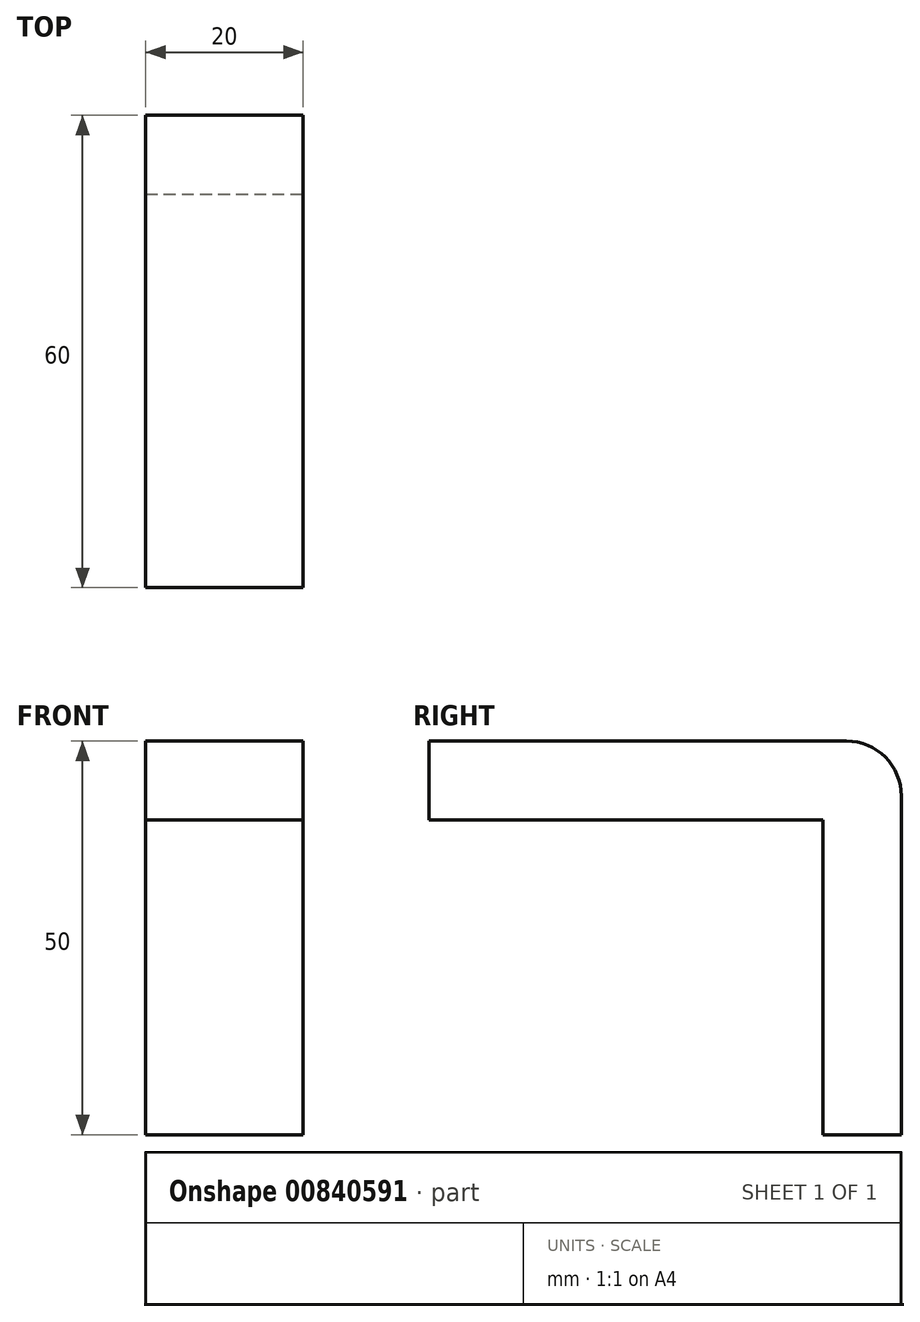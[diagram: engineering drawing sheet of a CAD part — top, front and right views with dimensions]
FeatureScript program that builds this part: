
annotation { "Feature Type Name" : "Feature", "Feature Type Description" : "" }
export const myFeature = defineFeature(function(context is Context, id is Id, definition is map)
    precondition{}
    {
        {
            var Q0;
            Q0=qCreatedBy(makeId("Front.planeOp"),FACE);
            var sketch = newSketch(context, id + "F0", { "sketchPlane" : qUnion([Q0])});
            skLineSegment(sketch, "E0.left", {"start": v(0, 0) * mm, "end": v(0, 0) * mm});
            skLineSegment(sketch, "E1", {"start": v(0, 0) * mm, "end": v(20, 0) * mm});
            skLineSegment(sketch, "E2", {"start": v(20, 0) * mm, "end": v(20, 50) * mm});
            skLineSegment(sketch, "E3", {"start": v(20, 50) * mm, "end": v(0, 50) * mm});
            skLineSegment(sketch, "E4", {"start": v(0, 50) * mm, "end": v(0, 0) * mm});
            skSolve(sketch);
        }
        {
            var Q0;
            Q0 = qSketchRegion(id + "F0", true);
            extrude(context, id + "F1", {"entities" : qUnion([Q0]), "depth" : 10 * mm, "offsetDistance" : 25 * mm});
        }
        {
            var Q0;
            Q0=makeQuery(id+"F1.opExtrude","CAP_FACE",FACE,{"disambiguationData":[OSD([sQuery(id+"F0.wireOp",EDGE,"E1"),sQuery(id+"F0.wireOp",EDGE,"E2"),sQuery(id+"F0.wireOp",EDGE,"E3"),sQuery(id+"F0.wireOp",EDGE,"E4")])],"isStart":false});
            var sketch = newSketch(context, id + "F2", { "sketchPlane" : qUnion([Q0])});
            skLineSegment(sketch, "E5.bottom", {"start": v(0, 50) * mm, "end": v(20, 50) * mm});
            skLineSegment(sketch, "E5.top", {"start": v(0, 40) * mm, "end": v(20, 40) * mm});
            skLineSegment(sketch, "E5.left", {"start": v(0, 50) * mm, "end": v(0, 40) * mm});
            skLineSegment(sketch, "E5.right", {"start": v(20, 50) * mm, "end": v(20, 40) * mm});
            skSolve(sketch);
        }
        {
            var Q0;
            Q0 = qSketchRegion(id + "F2", true);
            extrude(context, id + "F3", {"entities" : qUnion([Q0]), "operationType" : NewBodyOperationType.ADD, "depth" : 50 * mm, "offsetDistance" : 25 * mm});
        }
        {
            var Q0;
            Q0=makeQuery(id+"F1.opExtrude","CAP_EDGE",EDGE,{"disambiguationData":[OSD([sQuery(id+"F0.wireOp",EDGE,"E3")])],"isStart":true});
            var Q1;
            Q1=makeQuery(id+"F3.opExtrude","CAP_EDGE",EDGE,{"disambiguationData":[OSD([sQuery(id+"F2.wireOp",EDGE,"E5.top")])],"isStart":true});
            fillet(context, id + "F4", {"entities" : qUnion([Q0, Q1]), "radius" : 7 * mm, "tangentPropagation" : true, "allowEdgeOverflow" : false});
        }
    });
